# Revit family: IS_iLifeB_T4582_BIM_GB
name_source: partatom
category: Plumbing Fixtures
units: mm (PartAtom-declared; Revit-internal decimal feet)

## family parameters
Always vertical = No
Cut with Voids When Loaded = No
OmniClass Number = 23.45.05.14.27
OmniClass Title = Bidets
Part Type = Normal
Room Calculation Point = No
Round Connector Dimension = Use Diameter
Shared = No
Work Plane-Based = No

## types (1)
- T458201 - Ideal Standard i.life B back-to-wall bidet multi, wallfixation TT0293851, overflow round - White Finish
    AreaUnits = millimetres
    AssetType = Fixed
    BIMObjectName = IS_IdealStandard_Bidets_i.lifeB_T4582
    BIMobject category = Bidets
    BIMobject category code = sanitary-bidets
    BIMobject main category = Sanitary
    BIMobject main category code = sanitary
    BarCode = 8014140503651
    BidetMounting = L-shape floor fication
    Brand = Ideal Standard
    Brand url = http://www.idealstandard.co.uk
    Category = Sanitary
    Classification = bidets
    Color = White
    ConnectionType = Plumbing
    Cost = 0 $
    CurrencyUnit = £
    CurrentRevision = 1
    Date of publishing = 22/07/2022
    Description = Ideal Standard i.life B back-to-wall bidet multi, wallfixation TT0293851, overflow round, white, in carton box, EU pallet
    DurationUnit = Years
    Edition number = 1
    ElementType = Fixed
    ExpectedLife = 99
    Features = back-to-wall bidet multi, wallfixation TT0293851, overflow round, white, in carton box, EU pallet
    Finish = White
    GTIN code = https://8014140503651
    Help = https://www.idealstandard.co.uk
    IFC Classification = Sanitary Terminal
    IfcExportAs = IfcSanitaryTerminalType
    IfcExportType = BIDET
    Installation instructions = https://www.idealstandard.co.uk
    InstallationInstructions = https://www.idealstandard.co.uk
    LinearUnits = millimetres
    MainColor = White
    MaintenanceInformation = https://www.idealstandard.co.uk
    Manufacturer = Ideal Standard
    Manufacturer name = Ideal Standard
    ManufacturerURL = https://www.idealstandard.co.uk
    Material = Fireclay
    Material main = Fireclay
    Model = T458201
    ModelNumber = T458201
    ModelReference = Ideal Standard i.life B back-to-wall bidet multi, wallfixation TT0293851, overflow round
    NBS Reference Code = 45-35-70/320
    NBS Reference Description = Bidets
    Name = Bidets_i.lifeB_T4582_IdealStandard
    NettWeight = 25.5
    NominalDepth = 540 mm
    NominalHeight = 430 mm
    NominalLength = 540 mm
    NominalWidth = 354 mm
    OmniClass Code = 23-31 23 00
    OmniClass Description = Bidets
    PredefinedType = Bidets
    Product Guid = 37aecc30-5915-406e-8505-f74f64d390ac
    Product SKU = T4582
    Product certification = https://www.idealstandard.co.uk
    Product data url = https://bimobject.com
    Product family = I.Life B
    Product group = Sanitary
    Product name = I.Life b back-to-wall bidet multi, wall hung
    Product url = https://www.idealstandard.co.uk
    ProductInformation = https://www.idealstandard.co.uk
    QR code = http://bimobject.com
    Shape = sculptured
    Size = 355 x 540 x 430 mm
    Space = Internal
    SpareParts = https://www.idealstandard.co.uk
    Technical description = https://www.idealstandard.co.uk
    UNSPSC Code = 301815
    URL = https://www.idealstandard.co.uk
    Uniclass 2015 Code = Pr_40_20_06_11
    Uniclass 2015 Name = Bidets
    Uniclass2015Code = Pr_40_20_06_11
    Uniclass2015Title = Bidets
    Uniclass2015Version = v1.26
    Version = 1
    VolumeUnits = Liters
    WRASURL = https://www.wrasapprovals.co.uk
    WarrantyDescription = manufacturer warranty
    WarrantyDurationUnit = Years
    Weight Net (Kg) = 25.5
    Youtube clip = https://www.youtube.com

## geometry (parser evidence)
native form markers: Sweep x2
no freeform markers — native parametric forms only
